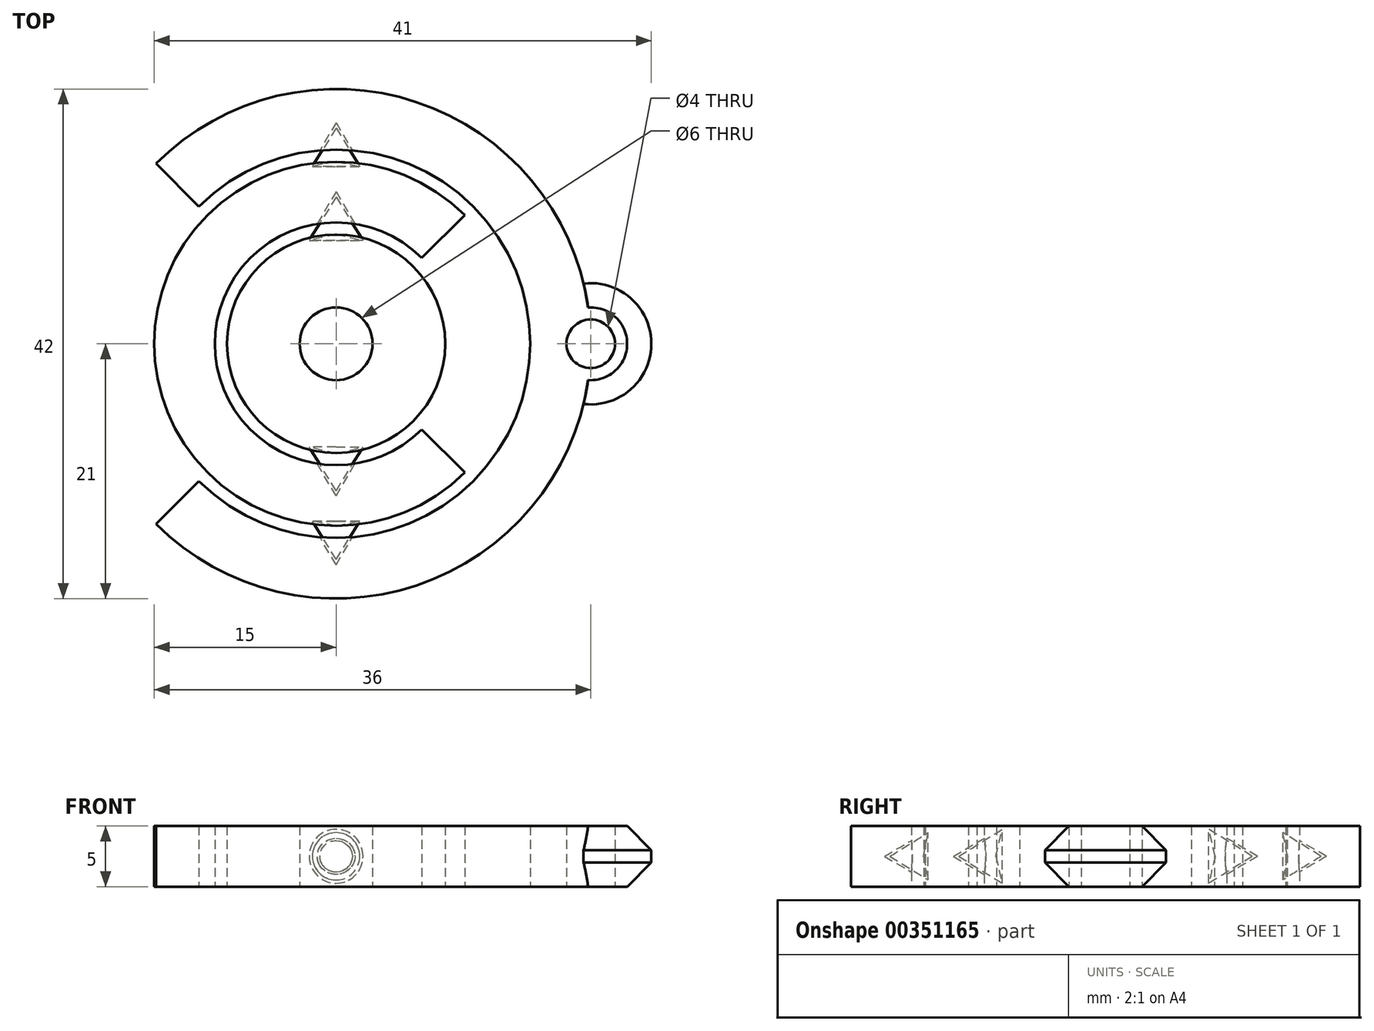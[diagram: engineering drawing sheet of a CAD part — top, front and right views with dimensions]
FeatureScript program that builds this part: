
annotation { "Feature Type Name" : "Feature", "Feature Type Description" : "" }
export const myFeature = defineFeature(function(context is Context, id is Id, definition is map)
    precondition{}
    {
        {
            var Q0;
            Q0=qCreatedBy(makeId("Top.planeOp"),FACE);
            var sketch = newSketch(context, id + "F0", { "sketchPlane" : qUnion([Q0])});
            skCircle(sketch, "E0", {"center": v(0, 0) * mm, "radius": 21 * mm});
            skCircle(sketch, "E1", {"center": v(0, 0) * mm, "radius": 15 * mm});
            skCircle(sketch, "E2", {"center": v(0, 0) * mm, "radius": 16 * mm});
            skCircle(sketch, "E3", {"center": v(0, 0) * mm, "radius": 10 * mm});
            skCircle(sketch, "E4", {"center": v(0, 0) * mm, "radius": 9 * mm});
            skCircle(sketch, "E5", {"center": v(0, 0) * mm, "radius": 3 * mm});
            skLineSegment(sketch, "E6.bottom", {"start": v(21, -21) * mm, "end": v(-21, -21) * mm});
            skLineSegment(sketch, "E6.top", {"start": v(21, 21) * mm, "end": v(-21, 21) * mm});
            skLineSegment(sketch, "E6.left", {"start": v(21, -21) * mm, "end": v(21, 21) * mm});
            skLineSegment(sketch, "E6.right", {"start": v(-21, -21) * mm, "end": v(-21, 21) * mm});
            skLineSegment(sketch, "E7", {"start": v(-21, 21) * mm, "end": v(21, -21) * mm});
            skLineSegment(sketch, "E8", {"start": v(0, -16) * mm, "end": v(0, -21) * mm});
            skLineSegment(sketch, "E9", {"start": v(16, 0) * mm, "end": v(21, 0) * mm});
            skPoint(sketch, "E9.startSnap0", {"position": v(21, 0) * mm});
            skLineSegment(sketch, "E10", {"start": v(0, 10) * mm, "end": v(0, 15) * mm});
            skLineSegment(sketch, "E11", {"start": v(-10, 0) * mm, "end": v(-15, 0) * mm});
            skCircle(sketch, "E12", {"center": v(-14.85, 14.85) * mm, "radius": 5 * mm});
            skCircle(sketch, "E13", {"center": v(-14.85, 14.85) * mm, "radius": 2 * mm});
            skSolve(sketch);
        }
        {
            var Q0;
            {var subQ0=sQuery(id+"F0.wireOp",EDGE,"E11");Q0=makeQuery(id+"F0.imprint","IMPRINT",FACE,{"disambiguationData":[TD([[makeQuery(id+"F0.imprint","IMPRINT",EDGE,{"derivedFrom":subQ0}),1.0]])]});}
            var Q1;
            {var subQ0=sQuery(id+"F0.wireOp",EDGE,"E10");Q1=makeQuery(id+"F0.imprint","IMPRINT",FACE,{"disambiguationData":[TD([[makeQuery(id+"F0.imprint","IMPRINT",EDGE,{"derivedFrom":subQ0}),-1.0]])]});}
            var Q2;
            {var subQ0=sQuery(id+"F0.wireOp",EDGE,"E7");var subQ1=sQuery(id+"F0.wireOp",EDGE,"E4");var subQ2=makeQuery(id+"F0.imprint","INTERSECT",VERTEX,{"disambiguationData":[OD(0.0)],"derivedFrom":[subQ1,subQ0]});Q2=makeQuery(id+"F0.imprint","IMPRINT",FACE,{"disambiguationData":[TD([[makeQuery(id+"F0.imprint","IMPRINT",EDGE,{"disambiguationData":[TD([[subQ2,-1.0]])],"derivedFrom":subQ1}),1.0]])]});}
            var Q3;
            {var subQ0=sQuery(id+"F0.wireOp",EDGE,"E7");var subQ1=sQuery(id+"F0.wireOp",EDGE,"E4");var subQ2=makeQuery(id+"F0.imprint","INTERSECT",VERTEX,{"disambiguationData":[OD(0.0)],"derivedFrom":[subQ1,subQ0]});Q3=makeQuery(id+"F0.imprint","IMPRINT",FACE,{"disambiguationData":[TD([[makeQuery(id+"F0.imprint","IMPRINT",EDGE,{"disambiguationData":[TD([[subQ2,1.0]])],"derivedFrom":subQ1}),1.0]])]});}
            var Q4;
            {var subQ5=sQuery(id+"F0.wireOp",EDGE,"E8");Q4=makeQuery(id+"F0.imprint","IMPRINT",FACE,{"disambiguationData":[TD([[makeQuery(id+"F0.imprint","IMPRINT",EDGE,{"derivedFrom":subQ5}),-1.0]])]});}
            var Q5;
            {var subQ6=sQuery(id+"F0.wireOp",EDGE,"E9");Q5=makeQuery(id+"F0.imprint","IMPRINT",FACE,{"disambiguationData":[TD([[makeQuery(id+"F0.imprint","IMPRINT",EDGE,{"derivedFrom":subQ6}),1.0]])]});}
            var Q6;
            {var subQ0=sQuery(id+"F0.wireOp",EDGE,"E12");var subQ1=sQuery(id+"F0.wireOp",EDGE,"E0");var subQ2=makeQuery(id+"F0.imprint","INTERSECT",VERTEX,{"disambiguationData":[OD(0.0)],"derivedFrom":[subQ1,subQ0]});Q6=makeQuery(id+"F0.imprint","IMPRINT",FACE,{"disambiguationData":[TD([[makeQuery(id+"F0.imprint","IMPRINT",EDGE,{"disambiguationData":[TD([[subQ2,-1.0]])],"derivedFrom":subQ1}),1.0]])]});}
            var Q7;
            {var subQ0=sQuery(id+"F0.wireOp",EDGE,"E13");var subQ1=sQuery(id+"F0.wireOp",EDGE,"E0");var subQ2=makeQuery(id+"F0.imprint","INTERSECT",VERTEX,{"disambiguationData":[OD(1.0)],"derivedFrom":[subQ1,subQ0]});Q7=makeQuery(id+"F0.imprint","IMPRINT",FACE,{"disambiguationData":[TD([[makeQuery(id+"F0.imprint","IMPRINT",EDGE,{"disambiguationData":[TD([[subQ2,-1.0]])],"derivedFrom":subQ1}),1.0]])]});}
            var Q8;
            {var subQ0=sQuery(id+"F0.wireOp",EDGE,"E13");var subQ1=sQuery(id+"F0.wireOp",EDGE,"E0");var subQ2=makeQuery(id+"F0.imprint","INTERSECT",VERTEX,{"disambiguationData":[OD(1.0)],"derivedFrom":[subQ1,subQ0]});Q8=makeQuery(id+"F0.imprint","IMPRINT",FACE,{"disambiguationData":[TD([[makeQuery(id+"F0.imprint","IMPRINT",EDGE,{"disambiguationData":[TD([[subQ2,-1.0]])],"derivedFrom":subQ1}),-1.0]])]});}
            var Q9;
            {var subQ0=sQuery(id+"F0.wireOp",EDGE,"E12");var subQ1=sQuery(id+"F0.wireOp",EDGE,"E0");var subQ2=makeQuery(id+"F0.imprint","INTERSECT",VERTEX,{"disambiguationData":[OD(0.0)],"derivedFrom":[subQ1,subQ0]});Q9=makeQuery(id+"F0.imprint","IMPRINT",FACE,{"disambiguationData":[TD([[makeQuery(id+"F0.imprint","IMPRINT",EDGE,{"disambiguationData":[TD([[subQ2,-1.0]])],"derivedFrom":subQ1}),-1.0]])]});}
            extrude(context, id + "F1", {"entities" : qUnion([Q0, Q1, Q2, Q3, Q4, Q5, Q6, Q7, Q8, Q9]), "depth" : 5 * mm, "symmetric" : true});
        }
        {
            var Q0;
            Q0=qCreatedBy(makeId("Front.planeOp"),FACE);
            var sketch = newSketch(context, id + "F2", { "sketchPlane" : qUnion([Q0])});
            skLineSegment(sketch, "E14", {"start": v(0, 50.47) * mm, "end": v(0, -46.34) * mm});
            skSolve(sketch);
        }
        {
            var Q0;
            Q0=makeQuery(id+"F1.opExtrude","SWEPT_BODY",BODY,{"disambiguationData":[OSD([sQuery(id+"F0.wireOp",EDGE,"E0"),sQuery(id+"F0.wireOp",EDGE,"E2"),sQuery(id+"F0.wireOp",EDGE,"E8"),sQuery(id+"F0.wireOp",EDGE,"E9"),sQuery(id+"F0.wireOp",EDGE,"E12"),sQuery(id+"F0.wireOp",EDGE,"E13")])]});
            var Q1;
            Q1=makeQuery(id+"F1.opExtrude","SWEPT_BODY",BODY,{"disambiguationData":[OSD([sQuery(id+"F0.wireOp",EDGE,"E1"),sQuery(id+"F0.wireOp",EDGE,"E3"),sQuery(id+"F0.wireOp",EDGE,"E10"),sQuery(id+"F0.wireOp",EDGE,"E11")])]});
            var Q2;
            Q2=makeQuery(id+"F1.opExtrude","SWEPT_BODY",BODY,{"disambiguationData":[OSD([sQuery(id+"F0.wireOp",EDGE,"E4"),sQuery(id+"F0.wireOp",EDGE,"E5")])]});
            var Q3;
            Q3=sQuery(id+"F2.wireOp",EDGE,"E14");
            transform(context, id + "F3", {"entities" : qUnion([Q0, Q1, Q2]), "transformType" : TransformType.ROTATION, "transformAxis" : qUnion([Q3]), "angle" : 135 * degree, "makeCopy" : false});
        }
        {
            var Q0;
            Q0=qCreatedBy(makeId("Top.planeOp"),FACE);
            var sketch = newSketch(context, id + "F4", { "sketchPlane" : qUnion([Q0])});
            skLineSegment(sketch, "E15", {"start": v(0, 9.05) * mm, "end": v(0, 12.1) * mm});
            skLineSegment(sketch, "E16", {"start": v(0, 12.1) * mm, "end": v(2.22, 8.52) * mm});
            skLineSegment(sketch, "E17", {"start": v(2.22, 8.52) * mm, "end": v(0, 9.05) * mm});
            skLineSegment(sketch, "E18", {"start": v(0, 15) * mm, "end": v(0, 17.78) * mm});
            skLineSegment(sketch, "E19", {"start": v(0, 17.78) * mm, "end": v(1.95, 14.62) * mm});
            skLineSegment(sketch, "E20", {"start": v(1.95, 14.62) * mm, "end": v(0, 15) * mm});
            skLineSegment(sketch, "E21.MirrorCS", {"start": v(0, -12.1) * mm, "end": v(2.22, -8.52) * mm});
            skLineSegment(sketch, "E22.MirrorCS", {"start": v(2.22, -8.52) * mm, "end": v(0, -9.05) * mm});
            skLineSegment(sketch, "E23.MirrorCS", {"start": v(0, -9.05) * mm, "end": v(0, -12.1) * mm});
            skLineSegment(sketch, "E24.MirrorCS", {"start": v(1.95, -14.62) * mm, "end": v(0, -15) * mm});
            skLineSegment(sketch, "E25.MirrorCS", {"start": v(0, -17.78) * mm, "end": v(1.95, -14.62) * mm});
            skLineSegment(sketch, "E26.MirrorCS", {"start": v(0, -15) * mm, "end": v(0, -17.78) * mm});
            skSolve(sketch);
        }
        {
            var Q0;
            Q0=makeQuery(id+"F4.imprint","IMPRINT",FACE,{"disambiguationData":[TD([[makeQuery(id+"F4.imprint","IMPRINT",EDGE,{"derivedFrom":sQuery(id+"F4.wireOp",EDGE,"E18")}),-1.0]])]});
            var Q1;
            Q1=makeQuery(id+"F4.imprint","IMPRINT",FACE,{"disambiguationData":[TD([[makeQuery(id+"F4.imprint","IMPRINT",EDGE,{"derivedFrom":sQuery(id+"F4.wireOp",EDGE,"E15")}),-1.0]])]});
            var Q2;
            Q2=makeQuery(id+"F4.imprint","IMPRINT",FACE,{"disambiguationData":[TD([[makeQuery(id+"F4.imprint","IMPRINT",EDGE,{"derivedFrom":sQuery(id+"F4.wireOp",EDGE,"E21.MirrorCS")}),1.0]])]});
            var Q3;
            Q3=makeQuery(id+"F4.imprint","IMPRINT",FACE,{"disambiguationData":[TD([[makeQuery(id+"F4.imprint","IMPRINT",EDGE,{"derivedFrom":sQuery(id+"F4.wireOp",EDGE,"E24.MirrorCS")}),1.0]])]});
            var Q4;
            Q4=sQuery(id+"F4.wireOp",EDGE,"E18");
            revolve(context, id + "F5", {"entities" : qUnion([Q0, Q1, Q2, Q3]), "axis" : qUnion([Q4]), "revolveType" : RevolveType.FULL});
        }
        {
            var Q0;
            Q0=qCreatedBy(makeId("Top.planeOp"),FACE);
            var sketch = newSketch(context, id + "F6", { "sketchPlane" : qUnion([Q0])});
            skLineSegment(sketch, "E27", {"start": v(0, 9.07) * mm, "end": v(0, 12.55) * mm});
            skLineSegment(sketch, "E28", {"start": v(0, 12.55) * mm, "end": v(2.32, 8.59) * mm});
            skLineSegment(sketch, "E29", {"start": v(2.32, 8.59) * mm, "end": v(0, 9.07) * mm});
            skLineSegment(sketch, "E30", {"start": v(0, 15.03) * mm, "end": v(0, 18.23) * mm});
            skLineSegment(sketch, "E31", {"start": v(0, 18.23) * mm, "end": v(2.02, 14.77) * mm});
            skLineSegment(sketch, "E32", {"start": v(2.02, 14.77) * mm, "end": v(0, 15.03) * mm});
            skLineSegment(sketch, "E33.MirrorCS", {"start": v(0, -12.55) * mm, "end": v(2.32, -8.59) * mm});
            skLineSegment(sketch, "E34.MirrorCS", {"start": v(0, -9.07) * mm, "end": v(0, -12.55) * mm});
            skLineSegment(sketch, "E35.MirrorCS", {"start": v(2.32, -8.59) * mm, "end": v(0, -9.07) * mm});
            skLineSegment(sketch, "E36.MirrorCS", {"start": v(0, -15.03) * mm, "end": v(0, -18.23) * mm});
            skLineSegment(sketch, "E37.MirrorCS", {"start": v(0, -18.23) * mm, "end": v(2.02, -14.77) * mm});
            skLineSegment(sketch, "E38.MirrorCS", {"start": v(2.02, -14.77) * mm, "end": v(0, -15.03) * mm});
            skSolve(sketch);
        }
        {
            var Q0;
            Q0 = qSketchRegion(id + "F6", true);
            var Q1;
            Q1=sQuery(id+"F6.wireOp",EDGE,"E27");
            revolve(context, id + "F7", {"entities" : qUnion([Q0]), "axis" : qUnion([Q1]), "revolveType" : RevolveType.FULL});
        }
        {
            var Q0;
            Q0=makeQuery(id+"F7.opRevolve","SWEPT_BODY",BODY,{"disambiguationData":[OSD([sQuery(id+"F6.wireOp",EDGE,"E30"),sQuery(id+"F6.wireOp",EDGE,"E31"),sQuery(id+"F6.wireOp",EDGE,"E32")])]});
            var Q1;
            Q1=makeQuery(id+"F7.opRevolve","SWEPT_BODY",BODY,{"disambiguationData":[OSD([sQuery(id+"F6.wireOp",EDGE,"E36.MirrorCS"),sQuery(id+"F6.wireOp",EDGE,"E37.MirrorCS"),sQuery(id+"F6.wireOp",EDGE,"E38.MirrorCS")])]});
            var Q2;
            Q2=makeQuery(id+"F1.opExtrude","SWEPT_BODY",BODY,{"disambiguationData":[OSD([sQuery(id+"F0.wireOp",EDGE,"E0"),sQuery(id+"F0.wireOp",EDGE,"E2"),sQuery(id+"F0.wireOp",EDGE,"E8"),sQuery(id+"F0.wireOp",EDGE,"E9"),sQuery(id+"F0.wireOp",EDGE,"E12"),sQuery(id+"F0.wireOp",EDGE,"E13")])]});
            booleanBodies(context, id + "F8", {"operationType" : BooleanOperationType.SUBTRACTION, "tools" : qUnion([Q0, Q1]), "targets" : qUnion([Q2])});
        }
        {
            var Q0;
            Q0=makeQuery(id+"F7.opRevolve","SWEPT_BODY",BODY,{"disambiguationData":[OSD([sQuery(id+"F6.wireOp",EDGE,"E27"),sQuery(id+"F6.wireOp",EDGE,"E28"),sQuery(id+"F6.wireOp",EDGE,"E29")])]});
            var Q1;
            Q1=makeQuery(id+"F7.opRevolve","SWEPT_BODY",BODY,{"disambiguationData":[OSD([sQuery(id+"F6.wireOp",EDGE,"E33.MirrorCS"),sQuery(id+"F6.wireOp",EDGE,"E34.MirrorCS"),sQuery(id+"F6.wireOp",EDGE,"E35.MirrorCS")])]});
            var Q2;
            Q2=makeQuery(id+"F1.opExtrude","SWEPT_BODY",BODY,{"disambiguationData":[OSD([sQuery(id+"F0.wireOp",EDGE,"E1"),sQuery(id+"F0.wireOp",EDGE,"E3"),sQuery(id+"F0.wireOp",EDGE,"E10"),sQuery(id+"F0.wireOp",EDGE,"E11")])]});
            booleanBodies(context, id + "F9", {"operationType" : BooleanOperationType.SUBTRACTION, "tools" : qUnion([Q0, Q1]), "targets" : qUnion([Q2])});
        }
        {
            var Q0;
            Q0=makeQuery(id+"F1.opExtrude","CAP_EDGE",EDGE,{"disambiguationData":[OSD([sQuery(id+"F0.wireOp",EDGE,"E12")])],"isStart":false});
            var Q1;
            Q1=makeQuery(id+"F1.opExtrude","CAP_EDGE",EDGE,{"disambiguationData":[OSD([sQuery(id+"F0.wireOp",EDGE,"E12")])],"isStart":true});
            chamfer(context, id + "F10", {"entities" : qUnion([Q0, Q1]), "width" : 2 * mm, "tangentPropagation" : true});
        }
    });
